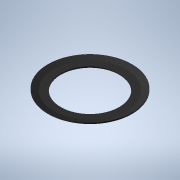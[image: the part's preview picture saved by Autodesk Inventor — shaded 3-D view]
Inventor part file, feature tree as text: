
AUTODESK INVENTOR PART (.ipt)
format: ipt  version: 2021 (Build 250183000, 183)  size: 126,976 bytes
history: native  units: mm
features: other x7, revolve x1, sketch x1
ambient origin geometry x8: Origin, YZ Plane, XZ Plane, XY Plane, X Axis, Y Axis, Z Axis, Center Point
bodies: Solid1 (feature_tree)
feature tree (9):
  revolve  "Revolution1"  [1 undecoded]
  other  "FL1_XY"
  other  "FL1_YZ"
  other  "FL1_ZX"
  other  "FL1_X"
  other  "FL1_Y"
  other  "FL1_Z"
  other  "FL1_Center"
  sketch  "Sketch_1"  dims[d0=360.0deg d1=0.0mm]
note: 1 required parameter value undecoded (feature->parameter linkage not recoverable at this tier; creation-order binding heuristic only, values carry confidence <= 0.55)
